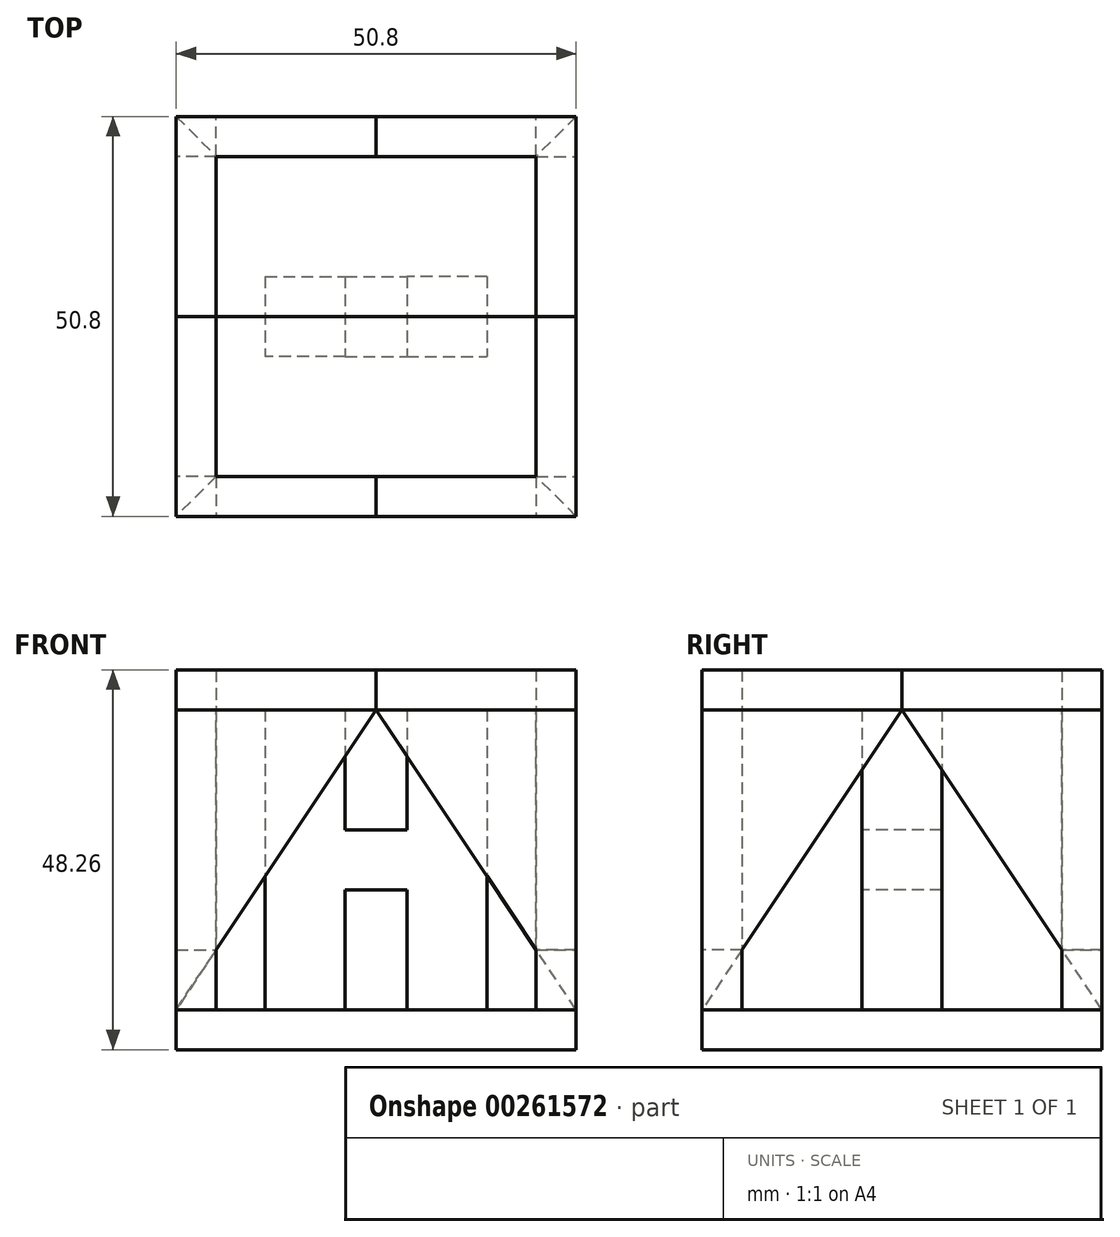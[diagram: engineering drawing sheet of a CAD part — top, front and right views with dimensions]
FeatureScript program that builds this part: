
annotation { "Feature Type Name" : "Feature", "Feature Type Description" : "" }
export const myFeature = defineFeature(function(context is Context, id is Id, definition is map)
    precondition{}
    {
        {
            var Q0;
            Q0=qCreatedBy(makeId("Top.planeOp"),FACE);
            var sketch = newSketch(context, id + "F0", { "sketchPlane" : qUnion([Q0])});
            skLineSegment(sketch, "E0.top", {"start": v(0, 25.4) * mm, "end": v(25.4, 25.4) * mm});
            skLineSegment(sketch, "E0.right", {"start": v(25.4, 0) * mm, "end": v(25.4, 25.4) * mm});
            skLineSegment(sketch, "E1.bottom", {"start": v(25.4, 25.4) * mm, "end": v(-25.4, 25.4) * mm});
            skLineSegment(sketch, "E1.top", {"start": v(25.4, -25.4) * mm, "end": v(-25.4, -25.4) * mm});
            skLineSegment(sketch, "E1.left", {"start": v(25.4, 25.4) * mm, "end": v(25.4, -25.4) * mm});
            skLineSegment(sketch, "E1.right", {"start": v(-25.4, 25.4) * mm, "end": v(-25.4, -25.4) * mm});
            skSolve(sketch);
        }
        {
            var Q0;
            {var subQ4=sQuery(id+"F0.wireOp",EDGE,"E1.top");Q0=makeQuery(id+"F0.imprint","IMPRINT",FACE,{"disambiguationData":[TD([[makeQuery(id+"F0.imprint","IMPRINT",EDGE,{"derivedFrom":subQ4}),-1.0]])]});}
            extrude(context, id + "F1", {"entities" : qUnion([Q0]), "depth" : 5.08 * mm});
        }
        {
            var Q0;
            Q0=makeQuery(id+"F1.opExtrude","SWEPT_FACE",FACE,{"disambiguationData":[OSD([sQuery(id+"F0.wireOp",EDGE,"E1.top")])]});
            var sketch = newSketch(context, id + "F2", { "sketchPlane" : qUnion([Q0])});
            skLineSegment(sketch, "E2", {"start": v(-25.4, 5.08) * mm, "end": v(-25.4, 43.18) * mm});
            skLineSegment(sketch, "E3", {"start": v(-25.4, 43.18) * mm, "end": v(0, 43.18) * mm});
            skLineSegment(sketch, "E4", {"start": v(0, 43.18) * mm, "end": v(-25.4, 5.08) * mm});
            skPoint(sketch, "E5.end.orphan", {"position": v(25.4, 43.18) * mm});
            skSolve(sketch);
        }
        {
            var Q0;
            Q0=makeQuery(id+"F2.imprint","IMPRINT",FACE,{"disambiguationData":[TD([[makeQuery(id+"F2.imprint","IMPRINT",EDGE,{"derivedFrom":sQuery(id+"F2.wireOp",EDGE,"E2")}),-1.0]])]});
            extrude(context, id + "F3", {"entities" : qUnion([Q0]), "oppositeDirection" : true, "depth" : 5.08 * mm});
        }
        {
            var Q0;
            Q0=makeQuery(id+"F1.opExtrude","SWEPT_FACE",FACE,{"disambiguationData":[OSD([sQuery(id+"F0.wireOp",EDGE,"E1.top")])]});
            var sketch = newSketch(context, id + "F4", { "sketchPlane" : qUnion([Q0])});
            skLineSegment(sketch, "E6", {"start": v(25.4, 5.08) * mm, "end": v(25.4, 43.18) * mm});
            skLineSegment(sketch, "E7", {"start": v(25.4, 43.18) * mm, "end": v(0, 43.18) * mm});
            skLineSegment(sketch, "E8", {"start": v(0, 43.18) * mm, "end": v(25.4, 5.08) * mm});
            skSolve(sketch);
        }
        {
            var Q0;
            Q0=makeQuery(id+"F4.imprint","IMPRINT",FACE,{"disambiguationData":[TD([[makeQuery(id+"F4.imprint","IMPRINT",EDGE,{"derivedFrom":sQuery(id+"F4.wireOp",EDGE,"E6")}),1.0]])]});
            extrude(context, id + "F5", {"entities" : qUnion([Q0]), "oppositeDirection" : true, "depth" : 5.08 * mm});
        }
        {
            var Q0;
            Q0=makeQuery(id+"F5.opExtrude","SWEPT_FACE",FACE,{"disambiguationData":[OSD([sQuery(id+"F4.wireOp",EDGE,"E6")])]});
            var sketch = newSketch(context, id + "F6", { "sketchPlane" : qUnion([Q0])});
            skLineSegment(sketch, "E9", {"start": v(-25.4, 43.18) * mm, "end": v(0, 43.18) * mm});
            skLineSegment(sketch, "E10", {"start": v(0, 43.18) * mm, "end": v(-25.4, 5.08) * mm});
            skSolve(sketch);
        }
        {
            var Q0;
            Q0=makeQuery(id+"F1.opExtrude","SWEPT_FACE",FACE,{"disambiguationData":[OSD([sQuery(id+"F0.wireOp",EDGE,"E1.left")])]});
            var sketch = newSketch(context, id + "F7", { "sketchPlane" : qUnion([Q0])});
            skLineSegment(sketch, "E11", {"start": v(25.4, 5.08) * mm, "end": v(25.4, 43.16) * mm});
            skLineSegment(sketch, "E12", {"start": v(25.4, 43.16) * mm, "end": v(0, 43.16) * mm});
            skLineSegment(sketch, "E13", {"start": v(0, 43.16) * mm, "end": v(25.4, 5.08) * mm});
            skSolve(sketch);
        }
        {
            var Q0;
            Q0=makeQuery(id+"F7.imprint","IMPRINT",FACE,{"disambiguationData":[TD([[makeQuery(id+"F7.imprint","IMPRINT",EDGE,{"derivedFrom":sQuery(id+"F7.wireOp",EDGE,"E11")}),1.0]])]});
            extrude(context, id + "F8", {"entities" : qUnion([Q0]), "oppositeDirection" : true, "depth" : 5.08 * mm});
        }
        {
            var Q0;
            Q0=makeQuery(id+"F8.opExtrude","SWEPT_FACE",FACE,{"disambiguationData":[OSD([sQuery(id+"F7.wireOp",EDGE,"E11")])]});
            var sketch = newSketch(context, id + "F9", { "sketchPlane" : qUnion([Q0])});
            skLineSegment(sketch, "E14", {"start": v(-25.4, 5.08) * mm, "end": v(-25.4, 43.16) * mm});
            skLineSegment(sketch, "E15", {"start": v(-25.4, 43.16) * mm, "end": v(0, 43.16) * mm});
            skLineSegment(sketch, "E16", {"start": v(0, 43.16) * mm, "end": v(-25.4, 5.08) * mm});
            skSolve(sketch);
        }
        {
            var Q0;
            Q0 = qSketchRegion(id + "F9", true);
            extrude(context, id + "F10", {"entities" : qUnion([Q0]), "operationType" : NewBodyOperationType.ADD, "oppositeDirection" : true, "depth" : 5.08 * mm});
        }
        {
            var Q0;
            Q0=makeQuery(id+"F1.opExtrude","SWEPT_FACE",FACE,{"disambiguationData":[OSD([sQuery(id+"F0.wireOp",EDGE,"E1.bottom")])]});
            var sketch = newSketch(context, id + "F11", { "sketchPlane" : qUnion([Q0])});
            skLineSegment(sketch, "E17", {"start": v(25.4, 5.08) * mm, "end": v(25.4, 43.16) * mm});
            skLineSegment(sketch, "E18", {"start": v(25.4, 43.16) * mm, "end": v(0, 43.16) * mm});
            skLineSegment(sketch, "E19", {"start": v(0, 43.16) * mm, "end": v(25.4, 5.08) * mm});
            skSolve(sketch);
        }
        {
            var Q0;
            Q0=makeQuery(id+"F11.imprint","IMPRINT",FACE,{"disambiguationData":[TD([[makeQuery(id+"F11.imprint","IMPRINT",EDGE,{"derivedFrom":sQuery(id+"F11.wireOp",EDGE,"E17")}),1.0]])]});
            extrude(context, id + "F12", {"entities" : qUnion([Q0]), "oppositeDirection" : true, "depth" : 5.08 * mm});
        }
        {
            var Q0;
            Q0=makeQuery(id+"F12.opExtrude","SWEPT_FACE",FACE,{"disambiguationData":[OSD([sQuery(id+"F11.wireOp",EDGE,"E17")])]});
            var sketch = newSketch(context, id + "F13", { "sketchPlane" : qUnion([Q0])});
            skLineSegment(sketch, "E20", {"start": v(-25.4, 5.08) * mm, "end": v(-25.4, 43.16) * mm});
            skLineSegment(sketch, "E21", {"start": v(-25.4, 43.16) * mm, "end": v(0, 43.16) * mm});
            skLineSegment(sketch, "E22", {"start": v(0, 43.16) * mm, "end": v(-25.4, 5.08) * mm});
            skSolve(sketch);
        }
        {
            var Q0;
            {var subQ0=sQuery(id+"F13.wireOp",EDGE,"E21");var subQ3=sQuery(id+"F13.wireOp",EDGE,"E22");var subQ4=makeQuery(id+"F13.imprint","INTERSECT",VERTEX,{"derivedFrom":[subQ0,subQ3]});Q0=makeQuery(id+"F13.imprint","IMPRINT",FACE,{"disambiguationData":[TD([[makeQuery(id+"F13.imprint","IMPRINT",EDGE,{"disambiguationData":[TD([[subQ4,1.0]])],"derivedFrom":subQ0}),-1.0]])]});}
            var Q1;
            {var subQ0=sQuery(id+"F13.wireOp",EDGE,"E20");Q1=makeQuery(id+"F13.imprint","IMPRINT",FACE,{"disambiguationData":[TD([[makeQuery(id+"F13.imprint","IMPRINT",EDGE,{"derivedFrom":subQ0}),-1.0]])]});}
            extrude(context, id + "F14", {"entities" : qUnion([Q0, Q1]), "operationType" : NewBodyOperationType.ADD, "oppositeDirection" : true, "depth" : 5.08 * mm});
        }
        {
            var Q0;
            {var subQ1=sQuery(id+"F4.wireOp",EDGE,"E6");var subQ2=makeQuery(id+"F5.opExtrude","CAP_EDGE",EDGE,{"disambiguationData":[OSD([subQ1])],"isStart":true});Q0=makeQuery(id+"F6.imprint","IMPRINT",FACE,{"disambiguationData":[TD([[makeQuery(id+"F6.imprint","IMPRINT",EDGE,{"derivedFrom":subQ2}),-1.0]])]});}
            var Q1;
            {var subQ0=sQuery(id+"F6.wireOp",EDGE,"E9");var subQ3=sQuery(id+"F6.wireOp",EDGE,"E10");var subQ4=makeQuery(id+"F6.imprint","INTERSECT",VERTEX,{"derivedFrom":[subQ0,subQ3]});Q1=makeQuery(id+"F6.imprint","IMPRINT",FACE,{"disambiguationData":[TD([[makeQuery(id+"F6.imprint","IMPRINT",EDGE,{"disambiguationData":[TD([[subQ4,1.0]])],"derivedFrom":subQ0}),-1.0]])]});}
            extrude(context, id + "F15", {"entities" : qUnion([Q0, Q1]), "operationType" : NewBodyOperationType.ADD, "oppositeDirection" : true, "depth" : 5.08 * mm});
        }
        {
            var Q0;
            Q0=makeQuery(id+"F3.opExtrude","SWEPT_FACE",FACE,{"disambiguationData":[OSD([sQuery(id+"F2.wireOp",EDGE,"E2")])]});
            var sketch = newSketch(context, id + "F16", { "sketchPlane" : qUnion([Q0])});
            skLineSegment(sketch, "E23", {"start": v(25.4, 5.08) * mm, "end": v(25.4, 43.18) * mm});
            skLineSegment(sketch, "E24", {"start": v(25.4, 43.18) * mm, "end": v(0, 43.18) * mm});
            skLineSegment(sketch, "E25", {"start": v(0, 43.18) * mm, "end": v(25.4, 5.08) * mm});
            skSolve(sketch);
        }
        {
            var Q0;
            {var subQ0=sQuery(id+"F16.wireOp",EDGE,"E24");var subQ3=sQuery(id+"F16.wireOp",EDGE,"E25");var subQ4=makeQuery(id+"F16.imprint","INTERSECT",VERTEX,{"derivedFrom":[subQ0,subQ3]});Q0=makeQuery(id+"F16.imprint","IMPRINT",FACE,{"disambiguationData":[TD([[makeQuery(id+"F16.imprint","IMPRINT",EDGE,{"disambiguationData":[TD([[subQ4,1.0]])],"derivedFrom":subQ0}),1.0]])]});}
            var Q1;
            {var subQ0=sQuery(id+"F16.wireOp",EDGE,"E23");Q1=makeQuery(id+"F16.imprint","IMPRINT",FACE,{"disambiguationData":[TD([[makeQuery(id+"F16.imprint","IMPRINT",EDGE,{"derivedFrom":subQ0}),1.0]])]});}
            extrude(context, id + "F17", {"entities" : qUnion([Q0, Q1]), "operationType" : NewBodyOperationType.ADD, "oppositeDirection" : true, "depth" : 5.08 * mm});
        }
        {
            var Q0;
            Q0=makeQuery(id+"F1.opExtrude","CAP_FACE",FACE,{"disambiguationData":[OSD([sQuery(id+"F0.wireOp",EDGE,"E1.bottom"),sQuery(id+"F0.wireOp",EDGE,"E1.top"),sQuery(id+"F0.wireOp",EDGE,"E1.left"),sQuery(id+"F0.wireOp",EDGE,"E1.right")])],"isStart":false});
            var sketch = newSketch(context, id + "F18", { "sketchPlane" : qUnion([Q0])});
            skPoint(sketch, "E26.endSnap0", {"position": v(-25.4, 0) * mm});
            skLineSegment(sketch, "E27", {"start": v(-3.92, 5.08) * mm, "end": v(-3.92, -5.09) * mm});
            skLineSegment(sketch, "E28", {"start": v(-3.92, -5.09) * mm, "end": v(-14.1, -5.09) * mm});
            skPoint(sketch, "E29.start.orphan", {"position": v(-14.1, 0) * mm});
            skLineSegment(sketch, "E30", {"start": v(-14.1, 5.08) * mm, "end": v(-3.92, 5.08) * mm});
            skLineSegment(sketch, "E31", {"start": v(-14.1, 5.08) * mm, "end": v(-14.1, -5.09) * mm});
            skLineSegment(sketch, "E32", {"start": v(14.05, 5.08) * mm, "end": v(3.9, 5.08) * mm});
            skLineSegment(sketch, "E33", {"start": v(3.9, 5.08) * mm, "end": v(3.9, -5.08) * mm});
            skLineSegment(sketch, "E34", {"start": v(3.9, -5.08) * mm, "end": v(14.06, -5.08) * mm});
            skLineSegment(sketch, "E35", {"start": v(14.05, 5.08) * mm, "end": v(14.06, -5.08) * mm});
            skSolve(sketch);
        }
        {
            var Q0;
            Q0 = qSketchRegion(id + "F18", true);
            extrude(context, id + "F19", {"entities" : qUnion([Q0]), "operationType" : NewBodyOperationType.ADD, "depth" : 38.1 * mm});
        }
        {
            var Q0;
            Q0=makeQuery(id+"F19.opExtrude","SWEPT_FACE",FACE,{"disambiguationData":[OSD([sQuery(id+"F18.wireOp",EDGE,"E35")])]});
            var sketch = newSketch(context, id + "F20", { "sketchPlane" : qUnion([Q0])});
            skLineSegment(sketch, "E36", {"start": v(-5.08, 27.94) * mm, "end": v(-5.08, 20.33) * mm});
            skLineSegment(sketch, "E37", {"start": v(5.07, 20.33) * mm, "end": v(5.07, 27.94) * mm});
            skPoint(sketch, "E38.orphan", {"position": v(0, 5.08) * mm});
            skPoint(sketch, "E39.start.orphan", {"position": v(0, 20.33) * mm});
            skLineSegment(sketch, "E40", {"start": v(5.07, 20.33) * mm, "end": v(-5.08, 20.33) * mm});
            skPoint(sketch, "E41.start.orphan", {"position": v(0, 27.94) * mm});
            skLineSegment(sketch, "E42", {"start": v(5.07, 27.94) * mm, "end": v(-5.08, 27.94) * mm});
            skLineSegment(sketch, "E43", {"start": v(-5.08, 20.33) * mm, "end": v(-5.08, 27.94) * mm});
            skSolve(sketch);
        }
        {
            var Q0;
            Q0=makeQuery(id+"F20.imprint","IMPRINT",FACE,{"disambiguationData":[TD([[makeQuery(id+"F20.imprint","IMPRINT",EDGE,{"derivedFrom":sQuery(id+"F20.wireOp",EDGE,"E37")}),-1.0]])]});
            extrude(context, id + "F21", {"entities" : qUnion([Q0]), "operationType" : NewBodyOperationType.ADD, "oppositeDirection" : true, "depth" : 25.4 * mm});
        }
        {
            var Q0;
            Q0=makeQuery(id+"F15.boolean.opBoolean","MERGE",FACE,{"derivedFrom":[makeQuery(id+"F5.opExtrude","SWEPT_FACE",FACE,{"disambiguationData":[OSD([sQuery(id+"F4.wireOp",EDGE,"E7")])]}),makeQuery(id+"F15.opExtrude","SWEPT_FACE",FACE,{"disambiguationData":[OSD([sQuery(id+"F6.wireOp",EDGE,"E9")])]})]});
            var Q1;
            Q1=makeQuery(id+"F10.boolean.opBoolean","MERGE",FACE,{"derivedFrom":[makeQuery(id+"F8.opExtrude","SWEPT_FACE",FACE,{"disambiguationData":[OSD([sQuery(id+"F7.wireOp",EDGE,"E12")])]}),makeQuery(id+"F10.opExtrude","SWEPT_FACE",FACE,{"disambiguationData":[OSD([sQuery(id+"F9.wireOp",EDGE,"E15")])]})]});
            var Q2;
            Q2=makeQuery(id+"F14.boolean.opBoolean","MERGE",FACE,{"derivedFrom":[makeQuery(id+"F12.opExtrude","SWEPT_FACE",FACE,{"disambiguationData":[OSD([sQuery(id+"F11.wireOp",EDGE,"E18")])]}),makeQuery(id+"F14.opExtrude","SWEPT_FACE",FACE,{"disambiguationData":[OSD([sQuery(id+"F13.wireOp",EDGE,"E21")])]})]});
            var Q3;
            Q3=makeQuery(id+"F17.boolean.opBoolean","MERGE",FACE,{"derivedFrom":[makeQuery(id+"F3.opExtrude","SWEPT_FACE",FACE,{"disambiguationData":[OSD([sQuery(id+"F2.wireOp",EDGE,"E3")])]}),makeQuery(id+"F17.opExtrude","SWEPT_FACE",FACE,{"disambiguationData":[OSD([sQuery(id+"F16.wireOp",EDGE,"E24")])]})]});
            extrude(context, id + "F22", {"entities" : qUnion([Q0, Q1, Q2, Q3]), "depth" : 5.08 * mm});
        }
        {
            var Q0;
            Q0=makeQuery(id+"F22.opExtrude","SWEPT_FACE",FACE,{"disambiguationData":[OSD([sQuery(id+"F6.wireOp",EDGE,"E9")])]});
            var Q1;
            {var subQ0=sQuery(id+"F7.wireOp",EDGE,"E12");Q1=makeQuery(id+"F22.opExtrude","SWEPT_FACE",FACE,{"disambiguationData":[OSD([subQ0]),TDD([makeQuery(id+"F8.opExtrude","CAP_EDGE",EDGE,{"disambiguationData":[OSD([subQ0])],"isStart":false})])]});}
            extrude(context, id + "F23", {"entities" : qUnion([Q0, Q1]), "depth" : 40.64 * mm});
        }
    });
